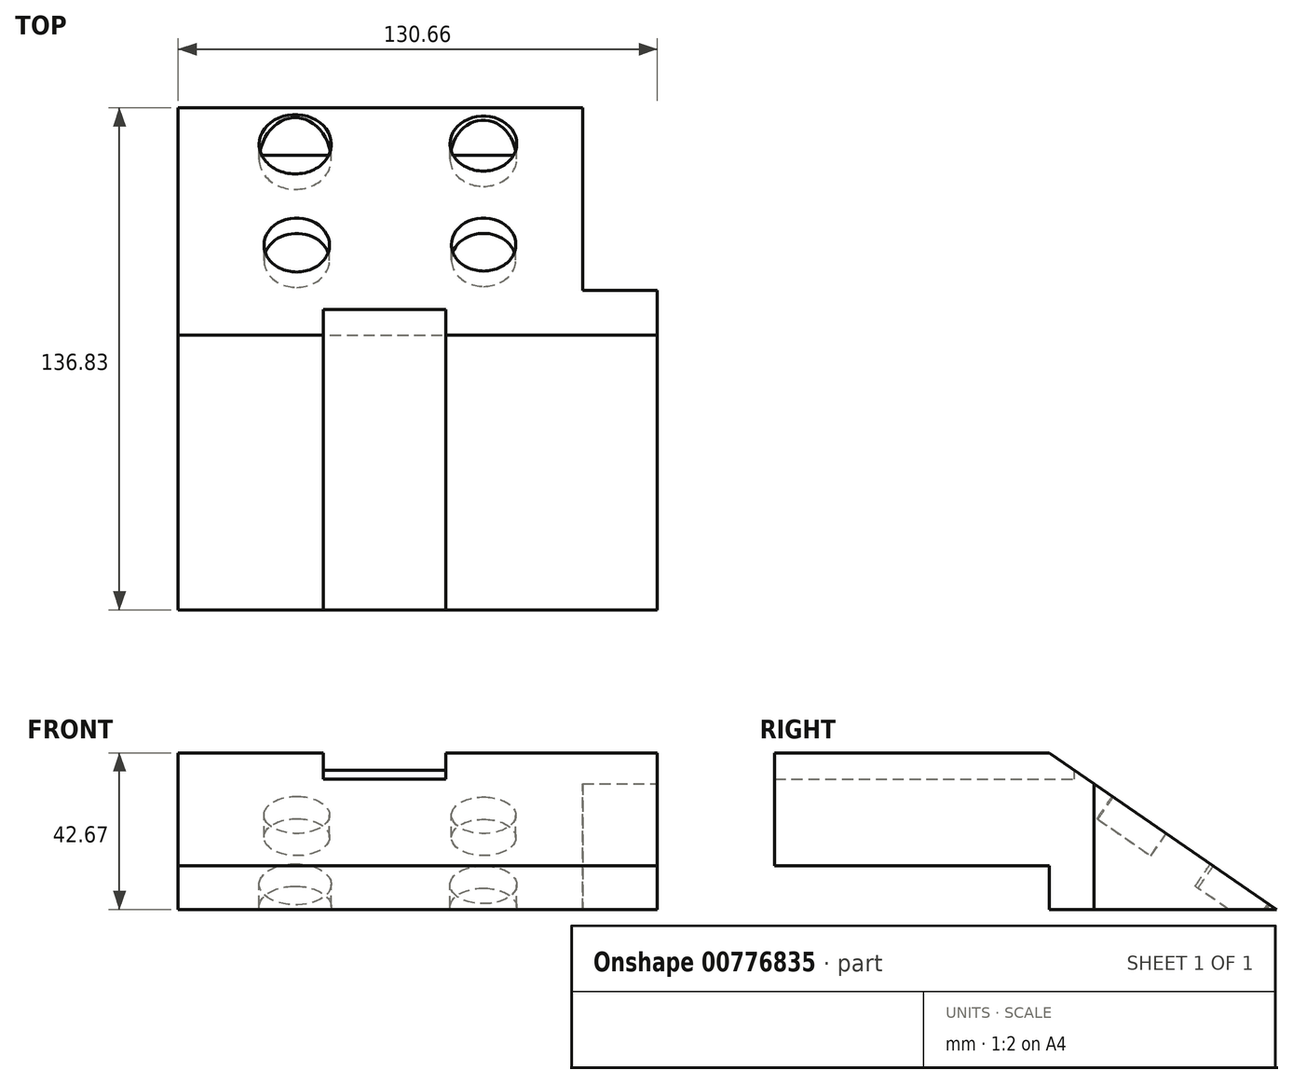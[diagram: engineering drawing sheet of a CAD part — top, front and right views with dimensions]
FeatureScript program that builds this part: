
annotation { "Feature Type Name" : "Feature", "Feature Type Description" : "" }
export const myFeature = defineFeature(function(context is Context, id is Id, definition is map)
    precondition{}
    {
        {
            var Q0;
            Q0=qCreatedBy(makeId("Top.planeOp"),FACE);
            var sketch = newSketch(context, id + "F0", { "sketchPlane" : qUnion([Q0])});
            skLineSegment(sketch, "E0.bottom", {"start": v(68.29, -74.89) * mm, "end": v(-62.37, -74.89) * mm});
            skLineSegment(sketch, "E0.top", {"start": v(68.29, 61.94) * mm, "end": v(-62.37, 61.94) * mm});
            skLineSegment(sketch, "E0.left", {"start": v(68.29, -74.89) * mm, "end": v(68.29, 61.94) * mm});
            skLineSegment(sketch, "E0.right", {"start": v(-62.37, -74.89) * mm, "end": v(-62.37, 61.94) * mm});
            skSolve(sketch);
        }
        {
            var Q0;
            Q0 = qSketchRegion(id + "F0", true);
            extrude(context, id + "F1", {"entities" : qUnion([Q0]), "depth" : 42.67 * mm, "offsetDistance" : 25.4 * mm});
        }
        {
            var Q0;
            Q0=makeQuery(id+"F1.opExtrude","SWEPT_FACE",FACE,{"disambiguationData":[OSD([sQuery(id+"F0.wireOp",EDGE,"E0.left")])]});
            var sketch = newSketch(context, id + "F2", { "sketchPlane" : qUnion([Q0])});
            skLineSegment(sketch, "E1", {"start": v(0, 42.67) * mm, "end": v(83.41, -14.78) * mm});
            skLineSegment(sketch, "E2", {"start": v(83.41, -14.78) * mm, "end": v(81.02, 51.47) * mm});
            skLineSegment(sketch, "E3", {"start": v(81.02, 51.47) * mm, "end": v(0, 42.67) * mm});
            skSolve(sketch);
        }
        {
            var Q0;
            Q0 = qSketchRegion(id + "F2", true);
            extrude(context, id + "F3", {"entities" : qUnion([Q0]), "operationType" : NewBodyOperationType.REMOVE, "oppositeDirection" : true, "depth" : 168.4 * mm, "offsetDistance" : 25.4 * mm});
        }
        {
            var Q0;
            Q0=makeQuery(id+"F1.opExtrude","CAP_FACE",FACE,{"disambiguationData":[OSD([sQuery(id+"F0.wireOp",EDGE,"E0.bottom"),sQuery(id+"F0.wireOp",EDGE,"E0.top"),sQuery(id+"F0.wireOp",EDGE,"E0.left"),sQuery(id+"F0.wireOp",EDGE,"E0.right")])],"isStart":false});
            var sketch = newSketch(context, id + "F4", { "sketchPlane" : qUnion([Q0])});
            skLineSegment(sketch, "E4.bottom", {"start": v(-22.73, -74.89) * mm, "end": v(10.6, -74.89) * mm});
            skLineSegment(sketch, "E4.top", {"start": v(-22.73, 6.95) * mm, "end": v(10.6, 6.95) * mm});
            skLineSegment(sketch, "E4.left", {"start": v(-22.73, -74.89) * mm, "end": v(-22.73, 6.95) * mm});
            skLineSegment(sketch, "E4.right", {"start": v(10.6, -74.89) * mm, "end": v(10.6, 6.95) * mm});
            skSolve(sketch);
        }
        {
            var Q0;
            Q0 = qSketchRegion(id + "F4", true);
            extrude(context, id + "F5", {"entities" : qUnion([Q0]), "operationType" : NewBodyOperationType.REMOVE, "oppositeDirection" : true, "depth" : 7.11 * mm, "offsetDistance" : 25.4 * mm});
        }
        {
            var Q0;
            Q0=makeQuery(id+"F1.opExtrude","SWEPT_FACE",FACE,{"disambiguationData":[OSD([sQuery(id+"F0.wireOp",EDGE,"E0.left")])]});
            var sketch = newSketch(context, id + "F6", { "sketchPlane" : qUnion([Q0])});
            skLineSegment(sketch, "E5", {"start": v(12.22, 34.26) * mm, "end": v(12.22, -9.62) * mm});
            skLineSegment(sketch, "E6", {"start": v(12.22, -9.62) * mm, "end": v(71.39, -9.62) * mm});
            skLineSegment(sketch, "E7", {"start": v(71.39, -9.62) * mm, "end": v(71.39, 35.84) * mm});
            skLineSegment(sketch, "E8", {"start": v(71.39, 35.84) * mm, "end": v(12.22, 34.26) * mm});
            skSolve(sketch);
        }
        {
            var Q0;
            Q0 = qSketchRegion(id + "F6", true);
            extrude(context, id + "F7", {"entities" : qUnion([Q0]), "operationType" : NewBodyOperationType.REMOVE, "oppositeDirection" : true, "depth" : 20.32 * mm, "offsetDistance" : 25.4 * mm});
        }
        {
            var Q0;
            Q0=makeQuery(id+"F1.opExtrude","SWEPT_FACE",FACE,{"disambiguationData":[OSD([sQuery(id+"F0.wireOp",EDGE,"E0.left")])]});
            var sketch = newSketch(context, id + "F8", { "sketchPlane" : qUnion([Q0])});
            skLineSegment(sketch, "E9.bottom", {"start": v(-74.89, 11.96) * mm, "end": v(0, 11.96) * mm});
            skLineSegment(sketch, "E9.top", {"start": v(-74.89, -2.67) * mm, "end": v(0, -2.67) * mm});
            skLineSegment(sketch, "E9.left", {"start": v(-74.89, 11.96) * mm, "end": v(-74.89, -2.67) * mm});
            skLineSegment(sketch, "E9.right", {"start": v(0, 11.96) * mm, "end": v(0, -2.67) * mm});
            skSolve(sketch);
        }
        {
            var Q0;
            Q0 = qSketchRegion(id + "F8", true);
            extrude(context, id + "F9", {"entities" : qUnion([Q0]), "operationType" : NewBodyOperationType.REMOVE, "oppositeDirection" : true, "depth" : 153.16 * mm, "offsetDistance" : 25.4 * mm});
        }
        {
            var Q0;
            Q0=makeQuery(id+"F3.boolean.opBoolean","COPY",FACE,{"derivedFrom":makeQuery(id+"F3.opExtrude","SWEPT_FACE",FACE,{"disambiguationData":[OSD([sQuery(id+"F2.wireOp",EDGE,"E1")])]})});
            var sketch = newSketch(context, id + "F10", { "sketchPlane" : qUnion([Q0])});
            skCircle(sketch, "E10", {"center": v(20.92, 5.76) * mm, "radius": 8.78 * mm});
            skCircle(sketch, "E11", {"center": v(-30.05, 5.6) * mm, "radius": 8.93 * mm});
            skCircle(sketch, "E12", {"center": v(20.85, 39.2) * mm, "radius": 9.09 * mm});
            skCircle(sketch, "E13", {"center": v(-30.45, 39) * mm, "radius": 9.84 * mm});
            skSolve(sketch);
        }
        {
            var Q0;
            Q0 = qSketchRegion(id + "F10", true);
            extrude(context, id + "F11", {"entities" : qUnion([Q0]), "operationType" : NewBodyOperationType.REMOVE, "oppositeDirection" : true, "depth" : 7.37 * mm, "offsetDistance" : 25.4 * mm});
        }
    });
